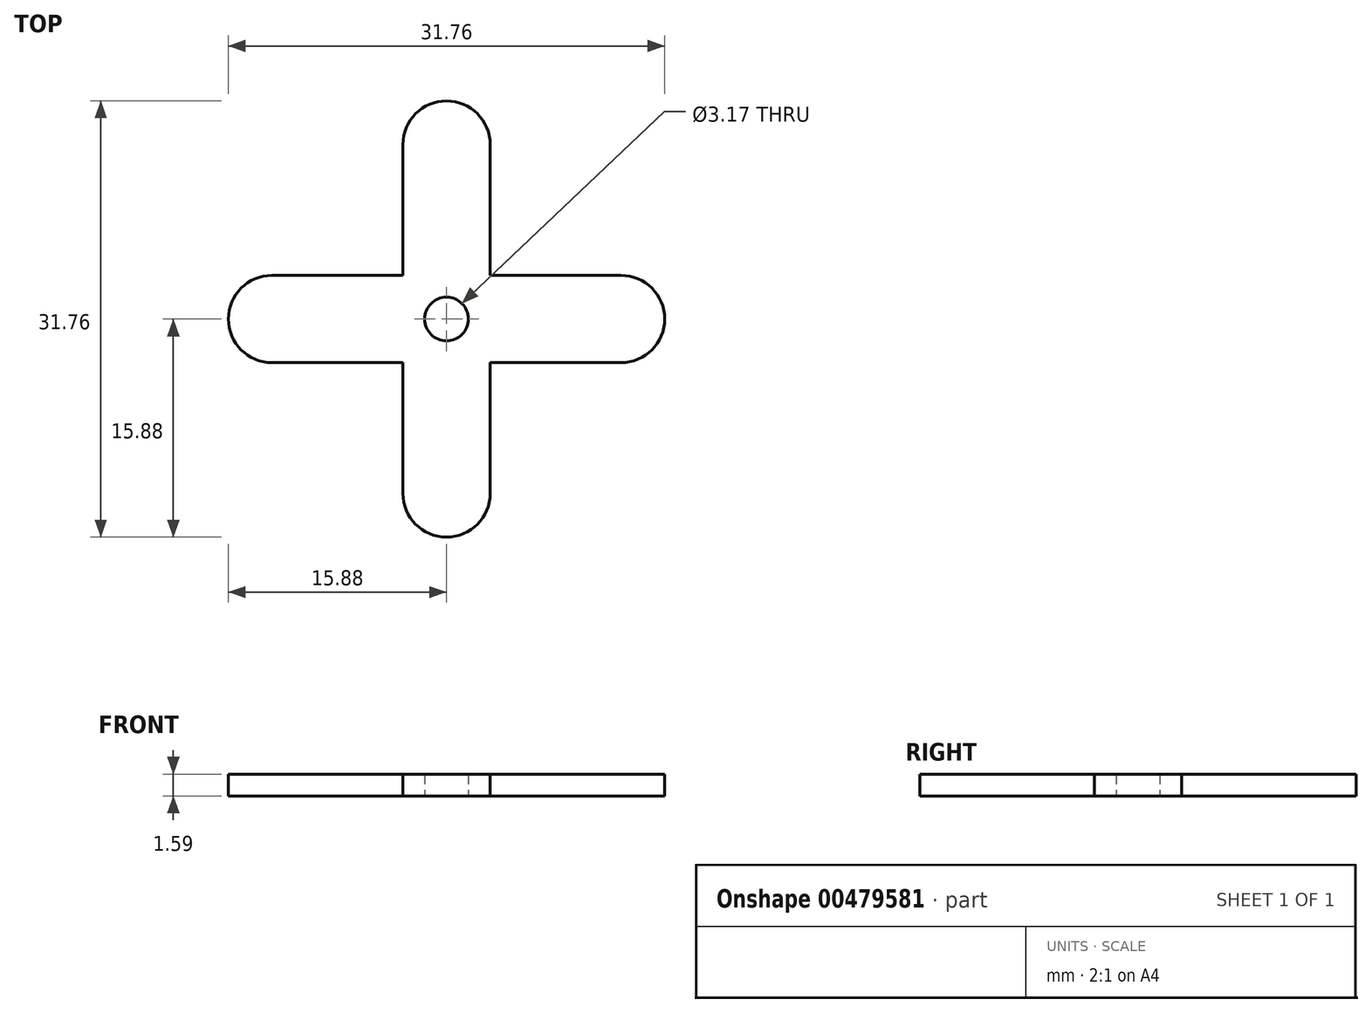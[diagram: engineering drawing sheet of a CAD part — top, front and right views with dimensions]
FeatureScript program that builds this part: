
annotation { "Feature Type Name" : "Feature", "Feature Type Description" : "" }
export const myFeature = defineFeature(function(context is Context, id is Id, definition is map)
    precondition{}
    {
        {
            var Q0;
            Q0=qCreatedBy(makeId("Top.planeOp"),FACE);
            var sketch = newSketch(context, id + "F0", { "sketchPlane" : qUnion([Q0])});
            skLineSegment(sketch, "E0.bottom", {"start": v(3.17, -12.7) * mm, "end": v(-3.18, -12.7) * mm});
            skLineSegment(sketch, "E0.top", {"start": v(3.18, 12.7) * mm, "end": v(-3.17, 12.7) * mm});
            skLineSegment(sketch, "E0.left", {"start": v(3.17, -12.7) * mm, "end": v(3.18, 12.7) * mm});
            skLineSegment(sketch, "E0.right", {"start": v(-3.18, -12.7) * mm, "end": v(-3.17, 12.7) * mm});
            skPoint(sketch, "E0.middle", {"position": v(0, 0) * mm});
            skLineSegment(sketch, "E1.bottom", {"start": v(12.7, -3.17) * mm, "end": v(-12.7, -3.18) * mm});
            skLineSegment(sketch, "E1.top", {"start": v(12.7, 3.18) * mm, "end": v(-12.7, 3.17) * mm});
            skLineSegment(sketch, "E1.left", {"start": v(12.7, -3.17) * mm, "end": v(12.7, 3.18) * mm});
            skLineSegment(sketch, "E1.right", {"start": v(-12.7, -3.18) * mm, "end": v(-12.7, 3.18) * mm});
            skCircle(sketch, "E2", {"center": v(0, 0) * mm, "radius": 1.59 * mm});
            skCircle(sketch, "E3", {"center": v(0, 12.7) * mm, "radius": 3.17 * mm});
            skCircle(sketch, "E4", {"center": v(-12.7, 0) * mm, "radius": 3.17 * mm});
            skCircle(sketch, "E5", {"center": v(0, -12.7) * mm, "radius": 3.18 * mm});
            skCircle(sketch, "E6", {"center": v(12.7, 0) * mm, "radius": 3.18 * mm});
            skSolve(sketch);
        }
        {
            var Q0;
            {var subQ0=sQuery(id+"F0.wireOp",EDGE,"E0.bottom");Q0=makeQuery(id+"F0.imprint","IMPRINT",FACE,{"disambiguationData":[TD([[makeQuery(id+"F0.imprint","IMPRINT",EDGE,{"derivedFrom":subQ0}),1.0]])]});}
            var Q1;
            {var subQ0=sQuery(id+"F0.wireOp",EDGE,"E0.bottom");Q1=makeQuery(id+"F0.imprint","IMPRINT",FACE,{"disambiguationData":[TD([[makeQuery(id+"F0.imprint","IMPRINT",EDGE,{"derivedFrom":subQ0}),-1.0]])]});}
            var Q2;
            {var subQ1=sQuery(id+"F0.wireOp",EDGE,"E0.left");var subQ4=sQuery(id+"F0.wireOp",EDGE,"E1.bottom");var subQ5=makeQuery(id+"F0.imprint","INTERSECT",VERTEX,{"derivedFrom":[subQ1,subQ4]});Q2=makeQuery(id+"F0.imprint","IMPRINT",FACE,{"disambiguationData":[TD([[makeQuery(id+"F0.imprint","IMPRINT",EDGE,{"disambiguationData":[TD([[subQ5,-1.0]])],"derivedFrom":subQ4}),1.0]])]});}
            var Q3;
            {var subQ0=sQuery(id+"F0.wireOp",EDGE,"E1.bottom");var subQ1=sQuery(id+"F0.wireOp",EDGE,"E0.right");var subQ2=makeQuery(id+"F0.imprint","INTERSECT",VERTEX,{"derivedFrom":[subQ1,subQ0]});Q3=makeQuery(id+"F0.imprint","IMPRINT",FACE,{"disambiguationData":[TD([[makeQuery(id+"F0.imprint","IMPRINT",EDGE,{"disambiguationData":[TD([[subQ2,-1.0]])],"derivedFrom":subQ1}),1.0]])]});}
            var Q4;
            {var subQ0=sQuery(id+"F0.wireOp",EDGE,"E1.bottom");var subQ1=sQuery(id+"F0.wireOp",EDGE,"E0.left");var subQ2=makeQuery(id+"F0.imprint","INTERSECT",VERTEX,{"derivedFrom":[subQ1,subQ0]});Q4=makeQuery(id+"F0.imprint","IMPRINT",FACE,{"disambiguationData":[TD([[makeQuery(id+"F0.imprint","IMPRINT",EDGE,{"disambiguationData":[TD([[subQ2,-1.0]])],"derivedFrom":subQ1}),-1.0]])]});}
            var Q5;
            {var subQ1=sQuery(id+"F0.wireOp",EDGE,"E0.left");var subQ4=sQuery(id+"F0.wireOp",EDGE,"E1.top");var subQ5=makeQuery(id+"F0.imprint","INTERSECT",VERTEX,{"derivedFrom":[subQ1,subQ4]});Q5=makeQuery(id+"F0.imprint","IMPRINT",FACE,{"disambiguationData":[TD([[makeQuery(id+"F0.imprint","IMPRINT",EDGE,{"disambiguationData":[TD([[subQ5,-1.0]])],"derivedFrom":subQ4}),-1.0]])]});}
            var Q6;
            Q6=makeQuery(id+"F0.imprint","IMPRINT",FACE,{"disambiguationData":[TD([[makeQuery(id+"F0.imprint","IMPRINT",EDGE,{"derivedFrom":sQuery(id+"F0.wireOp",EDGE,"E2")}),-1.0]])]});
            var Q7;
            {var subQ0=sQuery(id+"F0.wireOp",EDGE,"E1.right");Q7=makeQuery(id+"F0.imprint","IMPRINT",FACE,{"disambiguationData":[TD([[makeQuery(id+"F0.imprint","IMPRINT",EDGE,{"derivedFrom":subQ0}),1.0]])]});}
            var Q8;
            {var subQ0=sQuery(id+"F0.wireOp",EDGE,"E1.right");Q8=makeQuery(id+"F0.imprint","IMPRINT",FACE,{"disambiguationData":[TD([[makeQuery(id+"F0.imprint","IMPRINT",EDGE,{"derivedFrom":subQ0}),-1.0]])]});}
            var Q9;
            {var subQ0=sQuery(id+"F0.wireOp",EDGE,"E0.top");Q9=makeQuery(id+"F0.imprint","IMPRINT",FACE,{"disambiguationData":[TD([[makeQuery(id+"F0.imprint","IMPRINT",EDGE,{"derivedFrom":subQ0}),1.0]])]});}
            var Q10;
            {var subQ0=sQuery(id+"F0.wireOp",EDGE,"E0.top");Q10=makeQuery(id+"F0.imprint","IMPRINT",FACE,{"disambiguationData":[TD([[makeQuery(id+"F0.imprint","IMPRINT",EDGE,{"derivedFrom":subQ0}),-1.0]])]});}
            var Q11;
            {var subQ0=sQuery(id+"F0.wireOp",EDGE,"E1.left");Q11=makeQuery(id+"F0.imprint","IMPRINT",FACE,{"disambiguationData":[TD([[makeQuery(id+"F0.imprint","IMPRINT",EDGE,{"derivedFrom":subQ0}),-1.0]])]});}
            var Q12;
            {var subQ0=sQuery(id+"F0.wireOp",EDGE,"E1.left");Q12=makeQuery(id+"F0.imprint","IMPRINT",FACE,{"disambiguationData":[TD([[makeQuery(id+"F0.imprint","IMPRINT",EDGE,{"derivedFrom":subQ0}),1.0]])]});}
            extrude(context, id + "F1", {"entities" : qUnion([Q0, Q1, Q2, Q3, Q4, Q5, Q6, Q7, Q8, Q9, Q10, Q11, Q12]), "depth" : 1.59 * mm});
        }
    });
